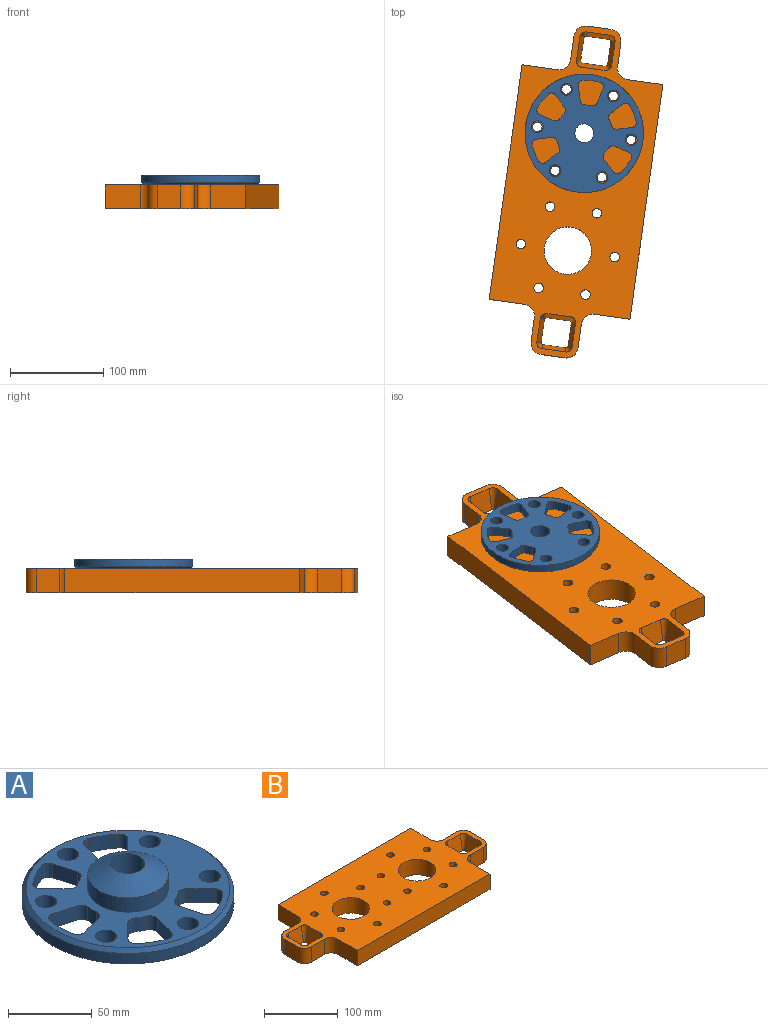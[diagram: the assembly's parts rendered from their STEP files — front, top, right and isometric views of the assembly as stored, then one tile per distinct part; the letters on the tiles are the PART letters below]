
ASSEMBLY  parts=2 mates=1
PART A: 53 faces, bbox 127x127x28.7 mm
  f0: cylinder r=10.16mm len=28.68mm, axis (0,0,-1), area 1830.8mm2, adj f1,f5
  f1: plane 127x127mm, normal (0,0,-1), area 8632.2mm2, adj f0,f2,f6,f7,f8,f9,f10,f11
  f2: cylinder r=63.5mm len=127mm, axis (0,0,-1), area 3040.2mm2, adj f1,f52
  f3: plane 121.92x121.92mm, normal (0,0,1), area 6134.1mm2, adj f4,f6,f7,f8,f9,f10,f11,f12
  f4: cylinder r=24.13mm len=48.26mm, axis (0,0,-1), area 1584.9mm2, adj f3,f5
  f5: cone r=24.13mm half-angle=60deg, axis (0,0,-1), area 1737.7mm2, adj f0,f4
  f6: cylinder r=6.35mm len=12.7mm, axis (0,0,1), area 405.4mm2, adj f1,f3
  f7: cylinder r=6.35mm len=12.7mm, axis (0,0,1), area 405.4mm2, adj f1,f3
  f8: cylinder r=6.35mm len=12.7mm, axis (0,0,1), area 405.4mm2, adj f1,f3
  f9: cylinder r=6.35mm len=12.7mm, axis (0,0,1), area 405.4mm2, adj f1,f3
  f10: cylinder r=6.35mm len=12.7mm, axis (0,0,1), area 405.4mm2, adj f1,f3
  f11: cylinder r=6.35mm len=12.7mm, axis (0,0,1), area 405.4mm2, adj f1,f3
  f12: plane 11.76x11.76mm, normal (-0.71,0.71,0), area 168.9mm2, adj f1,f3,f16,f19
  f13: cylinder r=57.15mm len=16.17mm, axis (0,0,1), area 190.5mm2, adj f1,f3,f16,f17
  f14: plane 16.06x10.16mm, normal (0.97,-0.26,0), area 168.9mm2, adj f1,f3,f17,f18
  f15: cylinder r=30.48mm len=10.16mm, axis (0,0,1), area 73.4mm2, adj f1,f3,f18,f19
  f16: cylinder r=5.08mm len=10.16mm, axis (0,0,1), area 86.1mm2, adj f1,f3,f12,f13
  f17: cylinder r=5.08mm len=10.16mm, axis (0,0,1), area 86.1mm2, adj f1,f3,f13,f14
  f18: cylinder r=5.08mm len=10.16mm, axis (0,0,1), area 73.7mm2, adj f1,f3,f14,f15
  f19: cylinder r=5.08mm len=10.16mm, axis (0,0,1), area 73.7mm2, adj f1,f3,f12,f15
  f20: plane 16.06x10.16mm, normal (-0.97,-0.26,0), area 168.9mm2, adj f1,f3,f24,f27
  f21: cylinder r=57.15mm len=16.17mm, axis (0,0,1), area 190.5mm2, adj f1,f3,f24,f25
  f22: plane 11.76x11.76mm, normal (0.71,0.71,0), area 168.9mm2, adj f1,f3,f25,f26
  f23: cylinder r=30.48mm len=10.16mm, axis (0,0,1), area 73.4mm2, adj f1,f3,f26,f27
  f24: cylinder r=5.08mm len=10.16mm, axis (0,0,1), area 86.1mm2, adj f1,f3,f20,f21
  f25: cylinder r=5.08mm len=10.16mm, axis (0,0,1), area 86.1mm2, adj f1,f3,f21,f22
  f26: cylinder r=5.08mm len=10.16mm, axis (0,0,1), area 73.7mm2, adj f1,f3,f22,f23
  f27: cylinder r=5.08mm len=10.16mm, axis (0,0,1), area 73.7mm2, adj f1,f3,f20,f23
  f28: plane 16.06x10.16mm, normal (-0.26,-0.97,0), area 168.9mm2, adj f1,f3,f32,f35
  f29: cylinder r=57.15mm len=18.67mm, axis (0,0,1), area 190.5mm2, adj f1,f3,f32,f33
  f30: plane 16.06x10.16mm, normal (-0.26,0.97,0), area 168.9mm2, adj f1,f3,f33,f34
  f31: cylinder r=30.48mm len=10.16mm, axis (0,0,1), area 73.4mm2, adj f1,f3,f34,f35
  f32: cylinder r=5.08mm len=10.16mm, axis (0,0,1), area 86.1mm2, adj f1,f3,f28,f29
  f33: cylinder r=5.08mm len=10.16mm, axis (0,0,1), area 86.1mm2, adj f1,f3,f29,f30
  f34: cylinder r=5.08mm len=10.16mm, axis (0,0,1), area 73.7mm2, adj f1,f3,f30,f31
  f35: cylinder r=5.08mm len=10.16mm, axis (0,0,1), area 73.7mm2, adj f1,f3,f28,f31
  f36: plane 11.76x11.76mm, normal (0.71,-0.71,0), area 168.9mm2, adj f1,f3,f40,f43
  f37: cylinder r=57.15mm len=16.17mm, axis (0,0,1), area 190.5mm2, adj f1,f3,f40,f41
  f38: plane 16.06x10.16mm, normal (-0.97,0.26,0), area 168.9mm2, adj f1,f3,f41,f42
  f39: cylinder r=30.48mm len=10.16mm, axis (0,0,1), area 73.4mm2, adj f1,f3,f42,f43
  f40: cylinder r=5.08mm len=10.16mm, axis (0,0,1), area 86.1mm2, adj f1,f3,f36,f37
  f41: cylinder r=5.08mm len=10.16mm, axis (0,0,1), area 86.1mm2, adj f1,f3,f37,f38
  f42: cylinder r=5.08mm len=10.16mm, axis (0,0,1), area 73.7mm2, adj f1,f3,f38,f39
  f43: cylinder r=5.08mm len=10.16mm, axis (0,0,1), area 73.7mm2, adj f1,f3,f36,f39
  f44: plane 16.06x10.16mm, normal (0.97,0.26,0), area 168.9mm2, adj f1,f3,f48,f51
  f45: cylinder r=57.15mm len=16.17mm, axis (0,0,1), area 190.5mm2, adj f1,f3,f48,f49
  f46: plane 11.76x11.76mm, normal (-0.71,-0.71,0), area 168.9mm2, adj f1,f3,f49,f50
  f47: cylinder r=30.48mm len=10.16mm, axis (0,0,1), area 73.4mm2, adj f1,f3,f50,f51
  f48: cylinder r=5.08mm len=10.16mm, axis (0,0,1), area 86.1mm2, adj f1,f3,f44,f45
  f49: cylinder r=5.08mm len=10.16mm, axis (0,0,1), area 86.1mm2, adj f1,f3,f45,f46
  f50: cylinder r=5.08mm len=10.16mm, axis (0,0,1), area 73.7mm2, adj f1,f3,f46,f47
  f51: cylinder r=5.08mm len=10.16mm, axis (0,0,1), area 73.7mm2, adj f1,f3,f44,f47
  f52: cone r=63.5mm half-angle=45deg, axis (0,0,-1), area 1404.5mm2, adj f2,f3
PART B: 52 faces, bbox 355.6x152.4x25.4 mm
  f0: plane 355.6x152.4mm, normal (0,0,1), area 36010.3mm2, adj f2,f3,f4,f5,f6,f7,f8,f9
  f1: plane 355.6x152.4mm, normal (0,0,-1), area 37151.8mm2, adj f2,f3,f4,f5,f6,f7,f8,f9
  f2: plane 25.4x25.4mm, normal (0,1,0), area 645.2mm2, adj f0,f1,f12,f13
  f3: plane 38.1x25.4mm, normal (1,0,0), area 967.7mm2, adj f0,f1,f4,f13
  f4: plane 254x25.4mm, normal (0,1,0), area 6451.6mm2, adj f0,f1,f3,f29
  f5: plane 254x25.4mm, normal (0,-1,0), area 6451.6mm2, adj f0,f1,f6,f30
  f6: plane 38.1x25.4mm, normal (1,0,0), area 967.7mm2, adj f0,f1,f5,f10
  f7: plane 25.4x25.4mm, normal (0,-1,0), area 645.2mm2, adj f0,f1,f10,f11
  f8: plane 25.4x25.4mm, normal (1,0,0), area 645.2mm2, adj f0,f1,f11,f12
  f9: cylinder r=25.4mm len=50.8mm, axis (0,0,-1), area 4053.7mm2, adj f0,f1
  f10: cylinder r=12.7mm len=25.4mm, axis (0,0,-1), area 506.7mm2, adj f0,f1,f6,f7
  f11: cylinder r=12.7mm len=25.4mm, axis (0,0,-1), area 506.7mm2, adj f0,f1,f7,f8
  f12: cylinder r=12.7mm len=25.4mm, axis (0,0,1), area 506.7mm2, adj f0,f1,f2,f8
  f13: cylinder r=12.7mm len=25.4mm, axis (0,0,1), area 506.7mm2, adj f0,f1,f2,f3
  f14: cylinder r=5.08mm len=25.4mm, axis (0,0,1), area 810.7mm2, adj f0,f1
  f15: cylinder r=5.08mm len=25.4mm, axis (0,0,1), area 810.7mm2, adj f0,f1
  f16: cylinder r=5.08mm len=25.4mm, axis (0,0,1), area 810.7mm2, adj f0,f1
  f17: cylinder r=5.08mm len=25.4mm, axis (0,0,1), area 810.7mm2, adj f0,f1
  f18: cylinder r=5.08mm len=25.4mm, axis (0,0,1), area 810.7mm2, adj f0,f1
  f19: cylinder r=5.08mm len=25.4mm, axis (0,0,1), area 810.7mm2, adj f0,f1
  f20: plane 25.4x25.4mm, normal (0.98,0,0.17), area 655.1mm2, adj f0,f1,f21,f27
  f21: cone r=6.35mm half-angle=10deg, axis (0,0,1), area 166.5mm2, adj f0,f1,f20,f22
  f22: plane 25.4x25.4mm, normal (0,0.98,0.17), area 655.1mm2, adj f0,f1,f21,f23
  f23: cone r=6.35mm half-angle=10deg, axis (0,0,1), area 166.5mm2, adj f0,f1,f22,f24
  f24: plane 25.4x25.4mm, normal (-0.98,0,0.17), area 655.1mm2, adj f0,f1,f23,f25
  f25: cone r=6.35mm half-angle=10deg, axis (0,0,1), area 166.5mm2, adj f0,f1,f24,f26
  f26: plane 25.4x25.4mm, normal (0,-0.98,0.17), area 655.1mm2, adj f0,f1,f25,f27
  f27: cone r=6.35mm half-angle=10deg, axis (0,0,1), area 166.5mm2, adj f0,f1,f20,f26
  f28: plane 25.4x25.4mm, normal (0,1,0), area 645.2mm2, adj f0,f1,f36,f37
  f29: plane 38.1x25.4mm, normal (-1,0,0), area 967.7mm2, adj f0,f1,f4,f37
  f30: plane 38.1x25.4mm, normal (-1,0,0), area 967.7mm2, adj f0,f1,f5,f34
  f31: plane 25.4x25.4mm, normal (0,-1,0), area 645.2mm2, adj f0,f1,f34,f35
  f32: plane 25.4x25.4mm, normal (-1,0,0), area 645.2mm2, adj f0,f1,f35,f36
  f33: cylinder r=25.4mm len=50.8mm, axis (0,0,-1), area 4053.7mm2, adj f0,f1
  f34: cylinder r=12.7mm len=25.4mm, axis (0,0,-1), area 506.7mm2, adj f0,f1,f30,f31
  f35: cylinder r=12.7mm len=25.4mm, axis (0,0,-1), area 506.7mm2, adj f0,f1,f31,f32
  f36: cylinder r=12.7mm len=25.4mm, axis (0,0,1), area 506.7mm2, adj f0,f1,f28,f32
  f37: cylinder r=12.7mm len=25.4mm, axis (0,0,1), area 506.7mm2, adj f0,f1,f28,f29
  f38: cylinder r=5.08mm len=25.4mm, axis (0,0,1), area 810.7mm2, adj f0,f1
  f39: cylinder r=5.08mm len=25.4mm, axis (0,0,1), area 810.7mm2, adj f0,f1
  f40: cylinder r=5.08mm len=25.4mm, axis (0,0,1), area 810.7mm2, adj f0,f1
  f41: cylinder r=5.08mm len=25.4mm, axis (0,0,1), area 810.7mm2, adj f0,f1
  f42: cylinder r=5.08mm len=25.4mm, axis (0,0,1), area 810.7mm2, adj f0,f1
  f43: cylinder r=5.08mm len=25.4mm, axis (0,0,1), area 810.7mm2, adj f0,f1
  f44: plane 25.4x25.4mm, normal (-0.98,0,0.17), area 655.1mm2, adj f0,f1,f45,f51
  f45: cone r=6.35mm half-angle=10deg, axis (0,0,1), area 166.5mm2, adj f0,f1,f44,f46
  f46: plane 25.4x25.4mm, normal (0,0.98,0.17), area 655.1mm2, adj f0,f1,f45,f47
  f47: cone r=6.35mm half-angle=10deg, axis (0,0,1), area 166.5mm2, adj f0,f1,f46,f48
  f48: plane 25.4x25.4mm, normal (0.98,0,0.17), area 655.1mm2, adj f0,f1,f47,f49
  f49: cone r=6.35mm half-angle=10deg, axis (0,0,1), area 166.5mm2, adj f0,f1,f48,f50
  f50: plane 25.4x25.4mm, normal (0,-0.98,0.17), area 655.1mm2, adj f0,f1,f49,f51
  f51: cone r=6.35mm half-angle=10deg, axis (0,0,1), area 166.5mm2, adj f0,f1,f44,f50
PLACE A rot(axis=(0.66,-0.75,0),180deg) t=(-130.13,-8.32,-2.58)mm
PLACE B rot(axis=(0,0,-1),98deg) t=(-147.79,-134.09,-38.14)mm
MATE revolute A.f0 <-> B.f33  axis (0,0,1) through (-130.13,-8.32,-12.74)mm
